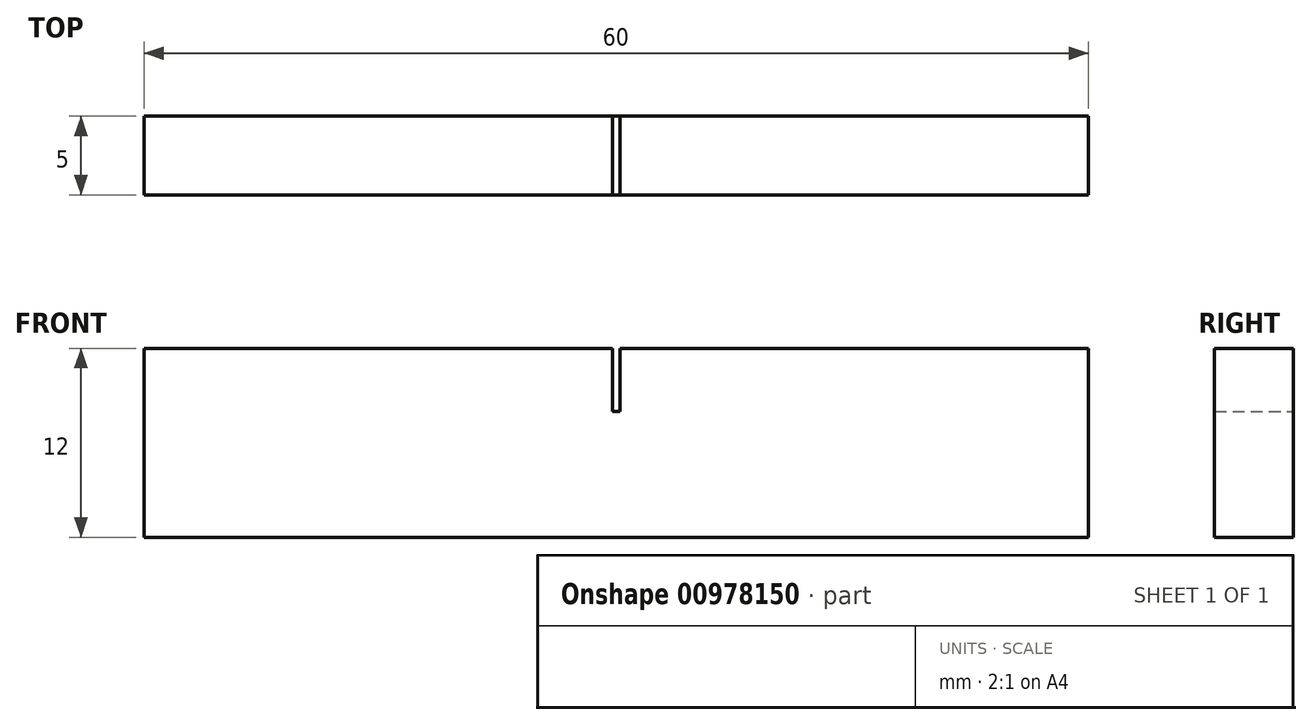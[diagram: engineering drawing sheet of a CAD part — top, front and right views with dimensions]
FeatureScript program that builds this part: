
annotation { "Feature Type Name" : "Feature", "Feature Type Description" : "" }
export const myFeature = defineFeature(function(context is Context, id is Id, definition is map)
    precondition{}
    {
        {
            var Q0;
            Q0=qCreatedBy(makeId("Front.planeOp"),FACE);
            var sketch = newSketch(context, id + "F0", { "sketchPlane" : qUnion([Q0])});
            skLineSegment(sketch, "E0.bottom", {"start": v(30, -6) * mm, "end": v(-30, -6) * mm});
            skLineSegment(sketch, "E0.top", {"start": v(30, 6) * mm, "end": v(0.25, 6) * mm});
            skLineSegment(sketch, "E0.left", {"start": v(30, -6) * mm, "end": v(30, 6) * mm});
            skLineSegment(sketch, "E0.right", {"start": v(-30, -6) * mm, "end": v(-30, 6) * mm});
            skPoint(sketch, "E0.middle", {"position": v(0, 0) * mm});
            skLineSegment(sketch, "E1.top", {"start": v(0.25, 2) * mm, "end": v(-0.25, 2) * mm});
            skLineSegment(sketch, "E1.left", {"start": v(0.25, 6) * mm, "end": v(0.25, 2) * mm});
            skLineSegment(sketch, "E1.right", {"start": v(-0.25, 6) * mm, "end": v(-0.25, 2) * mm});
            skPoint(sketch, "E1.middle", {"position": v(0, 4) * mm});
            skLineSegment(sketch, "E2.trimOffspring", {"start": v(-0.25, 6) * mm, "end": v(-30, 6) * mm});
            skSolve(sketch);
        }
        {
            var Q0;
            Q0 = qSketchRegion(id + "F0", true);
            extrude(context, id + "F1", {"entities" : qUnion([Q0]), "depth" : 5 * mm, "offsetDistance" : 25 * mm});
        }
    });
